# Revit family: Modern Plus
name_source: partatom
category: Mechanical Equipment
units: mm (PartAtom-declared; Revit-internal decimal feet)

## family parameters
Always vertical = Yes
Cut with Voids When Loaded = No
Host = Wall
OmniClass Number = 23.75.00.00
OmniClass Title = Climate Control (HVAC)
Part Type = Normal
Room Calculation Point = No
Round Connector Dimension = Use Diameter
Shared = No

## types (5) — shared parameters
Manufacturer = Masterwatt B.V.
URL = https://masterwatt.nl
Voltage = 230 V
zero-valued in all types: Default Elevation

## per-type parameters (varying)
| type | Art. No. | Model | Onder 1500 | Watt | boven 1500 |
| 0750 W | 429 754 211 | MDN 750 PLUS | Yes | 750 VA | No |
| 1000 W | 429 754 212 | MDN 1000 PLUS | Yes | 1000 VA | No |
| 1200 W | 429 754 213 | MDN 1200 PLUS | Yes | 1200 VA | No |
| 1500 W | 429 754 214 | MDN 1500 PLUS | No | 1500 VA | Yes |
| 2000 W | 429 754 216 | MDN 2000 PLUS | No | 2000 VA | Yes |

## geometry (parser evidence)
native form markers: Sweep x22
no freeform markers — native parametric forms only
